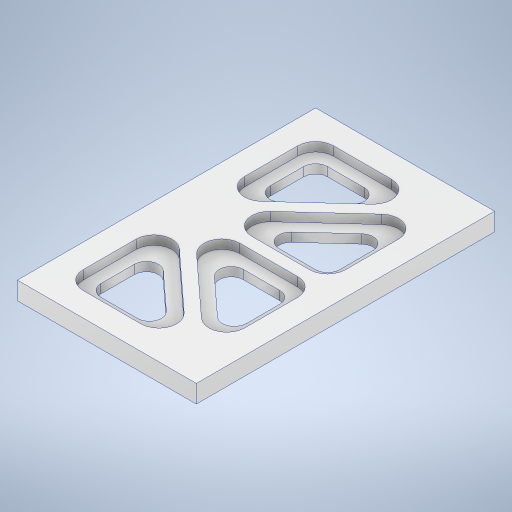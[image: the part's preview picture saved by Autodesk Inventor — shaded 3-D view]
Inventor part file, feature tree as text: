
AUTODESK INVENTOR PART (.ipt)
format: ipt  version: 2024 (Build 280153000, 153)  size: 370,688 bytes
history: native  units: mm
features: projected_geometry x6, extrude x3, fillet x2, sketch x2
ambient origin geometry x8: Origin, YZ Plane, XZ Plane, XY Plane, X Axis, Y Axis, Z Axis, Center Point
bodies: Solid1 (feature_tree)
feature tree (13):
  extrude  "Extrusion1"  Depth=120.0mm
  extrude  "Extrusion2"  Depth=12.0mm
  extrude  "Extrusion3"  Depth=12.0mm
  fillet  "Fillet1"  Radius=4.0mm
  fillet  "Fillet2"  Radius=4.0mm
  sketch  "Sketch1"  dims[d0=200.0mm d1=120.0mm]
  sketch  "Sketch2"  dims[d2=12.0mm d3=0.0mm d4=12.0mm d5=4.0mm d6=4.0mm d7=4.0mm d8=4.0mm d9=4.0mm d10=4.0mm d11=6.0mm d12=0.0mm d13=8.0mm d14=8.0mm d15=8.0mm d16=8.0mm d17=6.0mm d18=0.0mm d19=8.0mm d20=12.0mm]
  projected_geometry  "Projected Loop1"
  projected_geometry  "Projected Loop2"
  projected_geometry  "Projected Loop3"
  projected_geometry  "Projected Loop4"
  projected_geometry  "Projected Loop5"
  projected_geometry  "Projected Loop6"
